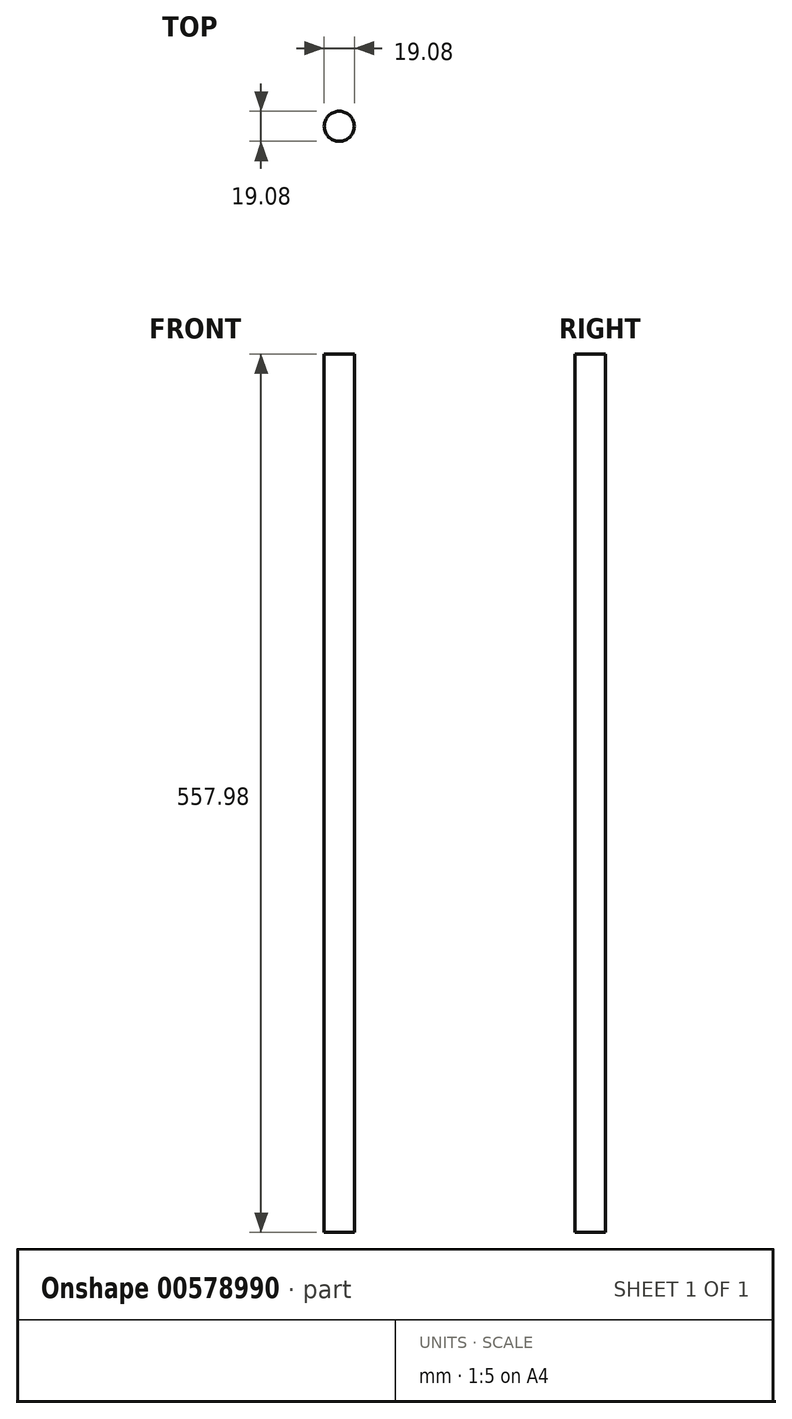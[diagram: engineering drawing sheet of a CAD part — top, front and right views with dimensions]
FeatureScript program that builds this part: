
annotation { "Feature Type Name" : "Feature", "Feature Type Description" : "" }
export const myFeature = defineFeature(function(context is Context, id is Id, definition is map)
    precondition{}
    {
        {
            var Q0;
            Q0=qCreatedBy(makeId("Front.planeOp"),FACE);
            var sketch = newSketch(context, id + "F0", { "sketchPlane" : qUnion([Q0])});
            skLineSegment(sketch, "E0", {"start": v(-61.87, 78.72) * mm, "end": v(-61.87, -479.26) * mm});
            skLineSegment(sketch, "E1", {"start": v(-61.87, -479.26) * mm, "end": v(-52.33, -479.26) * mm});
            skLineSegment(sketch, "E2", {"start": v(-52.33, -479.26) * mm, "end": v(-52.33, 78.72) * mm});
            skLineSegment(sketch, "E3", {"start": v(-52.33, 78.72) * mm, "end": v(-61.87, 78.72) * mm});
            skSolve(sketch);
        }
        {
            var Q0;
            Q0 = qSketchRegion(id + "F0", true);
            var Q1;
            Q1=sQuery(id+"F0.wireOp",EDGE,"E0");
            revolve(context, id + "F1", {"entities" : qUnion([Q0]), "axis" : qUnion([Q1]), "revolveType" : RevolveType.FULL});
        }
    });
